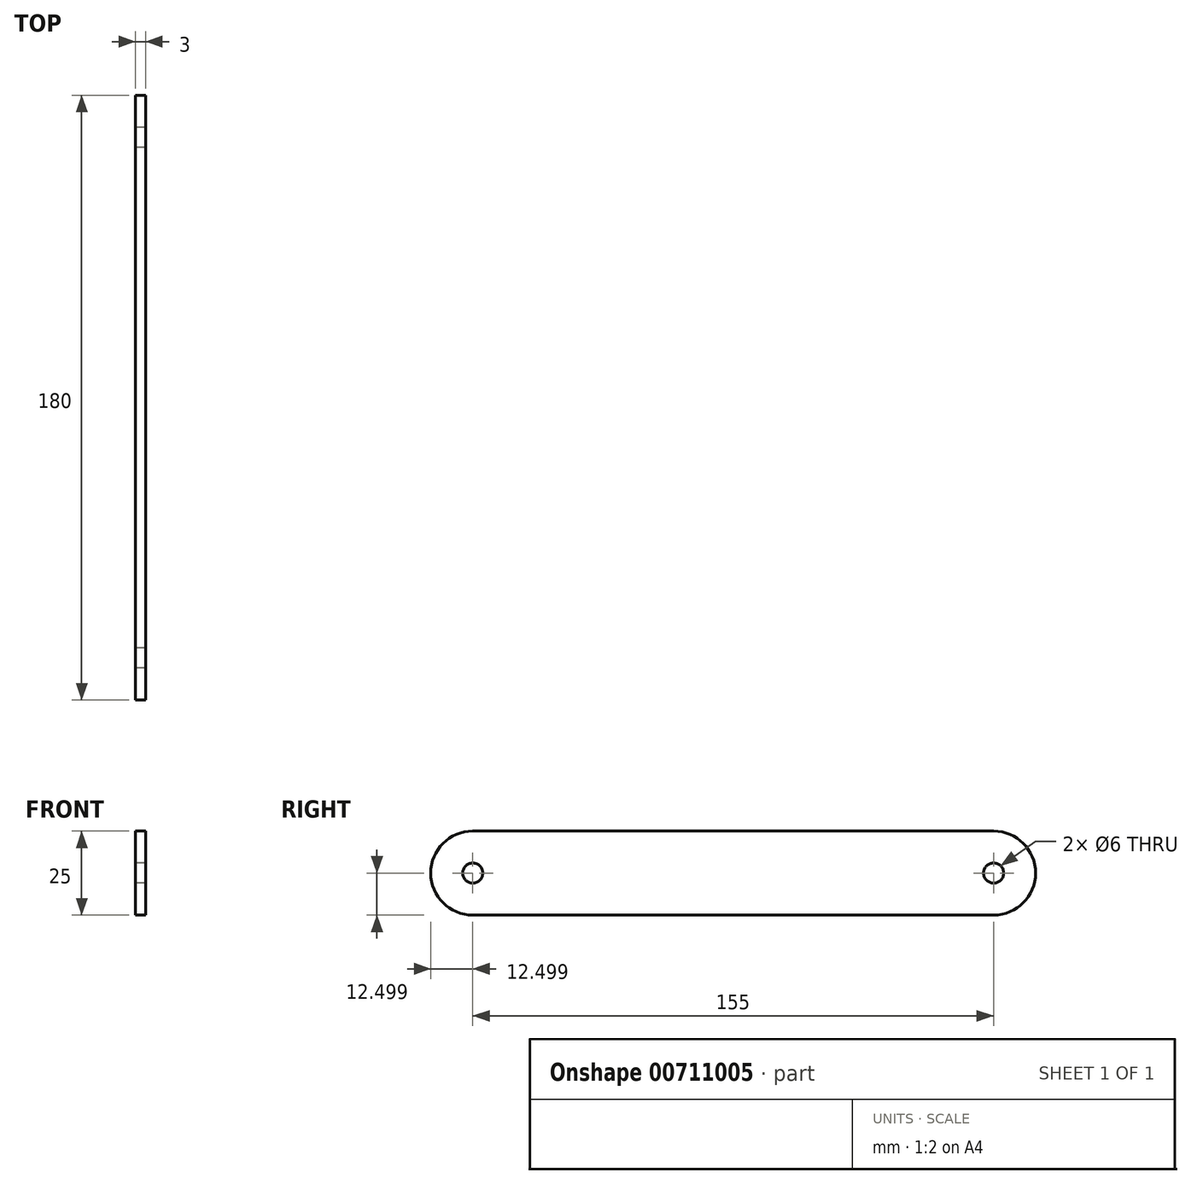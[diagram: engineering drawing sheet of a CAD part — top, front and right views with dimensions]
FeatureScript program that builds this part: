
annotation { "Feature Type Name" : "Feature", "Feature Type Description" : "" }
export const myFeature = defineFeature(function(context is Context, id is Id, definition is map)
    precondition{}
    {
        {
            var Q0;
            Q0=qCreatedBy(makeId("Right.planeOp"),FACE);
            var sketch = newSketch(context, id + "F0", { "sketchPlane" : qUnion([Q0])});
            skLineSegment(sketch, "E0.bottom", {"start": v(-85.4, 43.12) * mm, "end": v(69.6, 43.12) * mm});
            skLineSegment(sketch, "E0.top", {"start": v(-85.4, 18.12) * mm, "end": v(69.6, 18.12) * mm});
            skLineSegment(sketch, "E0.left", {"start": v(-97.9, 30.62) * mm, "end": v(-97.9, 30.62) * mm});
            skLineSegment(sketch, "E0.right", {"start": v(82.1, 30.62) * mm, "end": v(82.1, 30.62) * mm});
            skCircle(sketch, "E1", {"center": v(69.6, 30.62) * mm, "radius": 3 * mm});
            skLineSegment(sketch, "E2", {"start": v(-113.69, 30.62) * mm, "end": v(132.44, 30.62) * mm, "construction": true});
            skCircle(sketch, "E3", {"center": v(-85.4, 30.62) * mm, "radius": 3 * mm});
            skPoint(sketch, "E4.visualSharp", {"position": v(82.1, 43.12) * mm});
            skArc(sketch, "E4.filletArc", {"start": v(82.1, 30.62) * mm, "mid": v(78.44, 39.46) * mm, "end": v(69.6, 43.12) * mm});
            skPoint(sketch, "E5.visualSharp", {"position": v(82.1, 18.12) * mm});
            skArc(sketch, "E5.filletArc", {"start": v(69.6, 18.12) * mm, "mid": v(78.44, 21.78) * mm, "end": v(82.1, 30.62) * mm});
            skPoint(sketch, "E6.visualSharp", {"position": v(-97.9, 43.12) * mm});
            skArc(sketch, "E6.filletArc", {"start": v(-85.4, 43.12) * mm, "mid": v(-94.24, 39.46) * mm, "end": v(-97.9, 30.62) * mm});
            skPoint(sketch, "E7.visualSharp", {"position": v(-97.9, 18.12) * mm});
            skArc(sketch, "E7.filletArc", {"start": v(-97.9, 30.62) * mm, "mid": v(-94.24, 21.78) * mm, "end": v(-85.4, 18.12) * mm});
            skSolve(sketch);
        }
        {
            var Q0;
            Q0=makeQuery(id+"F0.imprint","IMPRINT",FACE,{"disambiguationData":[TD([[makeQuery(id+"F0.imprint","IMPRINT",EDGE,{"derivedFrom":sQuery(id+"F0.wireOp",EDGE,"E0.bottom")}),-1.0]])]});
            extrude(context, id + "F1", {"entities" : qUnion([Q0]), "depth" : 3 * mm, "offsetDistance" : 25 * mm});
        }
    });
